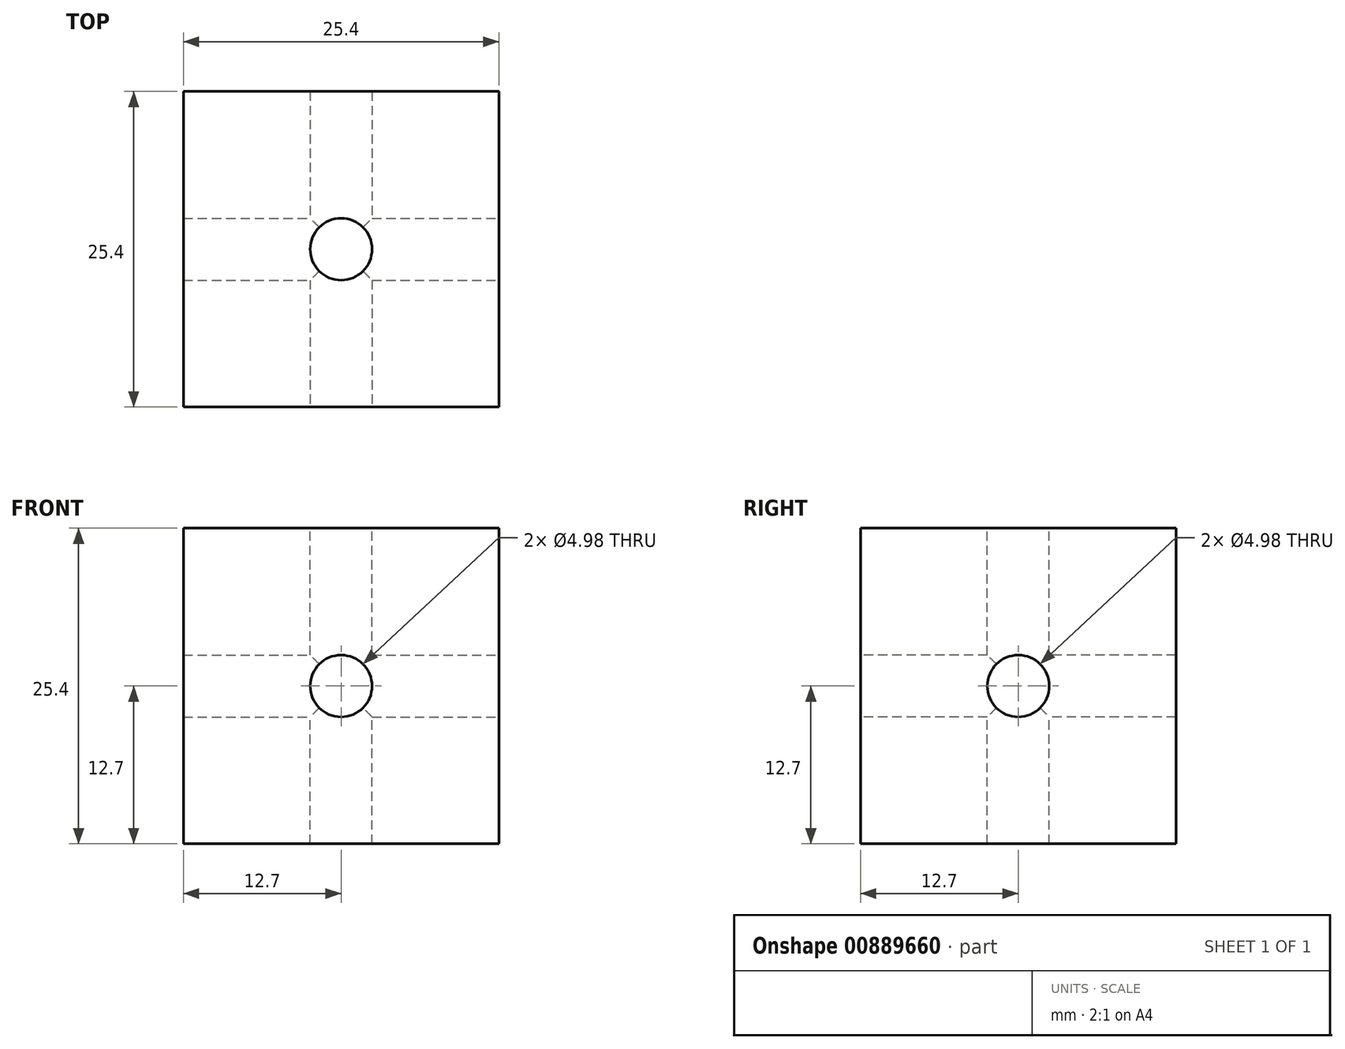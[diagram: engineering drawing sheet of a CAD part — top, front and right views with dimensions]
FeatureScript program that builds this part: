
annotation { "Feature Type Name" : "Feature", "Feature Type Description" : "" }
export const myFeature = defineFeature(function(context is Context, id is Id, definition is map)
    precondition{}
    {
        {
            var Q0;
            Q0=qCreatedBy(makeId("Top.planeOp"),FACE);
            var sketch = newSketch(context, id + "F0", { "sketchPlane" : qUnion([Q0])});
            skLineSegment(sketch, "E0.bottom", {"start": v(0, 0) * mm, "end": v(25.4, 0) * mm});
            skLineSegment(sketch, "E0.top", {"start": v(0, 25.4) * mm, "end": v(25.4, 25.4) * mm});
            skLineSegment(sketch, "E0.left", {"start": v(0, 0) * mm, "end": v(0, 25.4) * mm});
            skLineSegment(sketch, "E0.right", {"start": v(25.4, 0) * mm, "end": v(25.4, 25.4) * mm});
            skSolve(sketch);
        }
        {
            var Q0;
            Q0 = qSketchRegion(id + "F0", true);
            extrude(context, id + "F1", {"entities" : qUnion([Q0]), "depth" : 25.4 * mm, "offsetDistance" : 25.4 * mm});
        }
        {
            var Q0;
            Q0=makeQuery(id+"F1.opExtrude","CAP_FACE",FACE,{"disambiguationData":[OSD([sQuery(id+"F0.wireOp",EDGE,"E0.bottom"),sQuery(id+"F0.wireOp",EDGE,"E0.top"),sQuery(id+"F0.wireOp",EDGE,"E0.left"),sQuery(id+"F0.wireOp",EDGE,"E0.right")])],"isStart":false});
            var sketch = newSketch(context, id + "F2", { "sketchPlane" : qUnion([Q0])});
            skCircle(sketch, "E1", {"center": v(12.7, 12.7) * mm, "radius": 2.49 * mm});
            skPoint(sketch, "E1.centerSnap0", {"position": v(12.7, 0) * mm});
            skPoint(sketch, "E1.centerSnap1", {"position": v(0, 12.7) * mm});
            skSolve(sketch);
        }
        {
            var Q0;
            Q0 = qSketchRegion(id + "F2", true);
            extrude(context, id + "F3", {"entities" : qUnion([Q0]), "operationType" : NewBodyOperationType.REMOVE, "oppositeDirection" : true, "depth" : 25.4 * mm, "offsetDistance" : 25.4 * mm});
        }
        {
            var Q0;
            Q0=makeQuery(id+"F1.opExtrude","SWEPT_FACE",FACE,{"disambiguationData":[OSD([sQuery(id+"F0.wireOp",EDGE,"E0.right")])]});
            var sketch = newSketch(context, id + "F4", { "sketchPlane" : qUnion([Q0])});
            skCircle(sketch, "E2", {"center": v(12.7, 12.7) * mm, "radius": 2.49 * mm});
            skPoint(sketch, "E2.centerSnap0", {"position": v(0, 12.7) * mm});
            skPoint(sketch, "E2.centerSnap1", {"position": v(12.7, 25.4) * mm});
            skSolve(sketch);
        }
        {
            var Q0;
            Q0 = qSketchRegion(id + "F4", true);
            extrude(context, id + "F5", {"entities" : qUnion([Q0]), "operationType" : NewBodyOperationType.REMOVE, "oppositeDirection" : true, "depth" : 25.4 * mm, "offsetDistance" : 25.4 * mm});
        }
        {
            var Q0;
            Q0=makeQuery(id+"F1.opExtrude","SWEPT_FACE",FACE,{"disambiguationData":[OSD([sQuery(id+"F0.wireOp",EDGE,"E0.bottom")])]});
            var sketch = newSketch(context, id + "F6", { "sketchPlane" : qUnion([Q0])});
            skCircle(sketch, "E3", {"center": v(12.7, 12.7) * mm, "radius": 2.49 * mm});
            skPoint(sketch, "E3.centerSnap0", {"position": v(12.7, 0) * mm});
            skPoint(sketch, "E3.centerSnap1", {"position": v(0, 12.7) * mm});
            skSolve(sketch);
        }
        {
            var Q0;
            Q0 = qSketchRegion(id + "F6", true);
            extrude(context, id + "F7", {"entities" : qUnion([Q0]), "operationType" : NewBodyOperationType.REMOVE, "oppositeDirection" : true, "depth" : 25.4 * mm, "offsetDistance" : 25.4 * mm});
        }
    });
